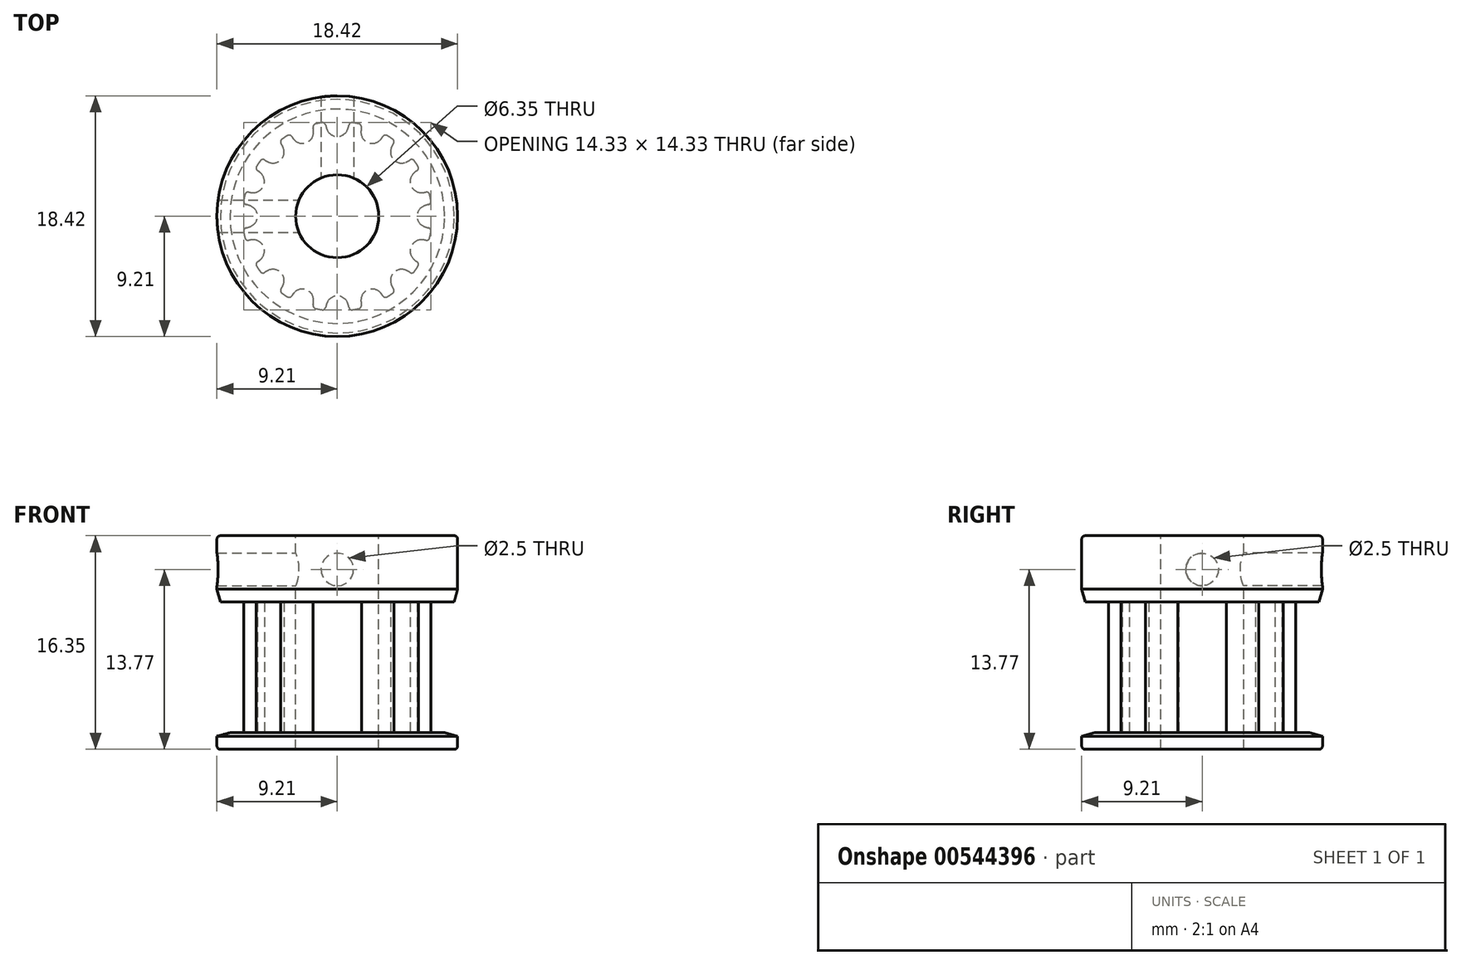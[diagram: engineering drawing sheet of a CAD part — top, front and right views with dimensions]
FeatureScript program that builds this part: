
annotation { "Feature Type Name" : "Feature", "Feature Type Description" : "" }
export const myFeature = defineFeature(function(context is Context, id is Id, definition is map)
    precondition{}
    {
        {
            assignVariable(context, id + "F0", {"name" : "teeth", "anyValue" : 16});
        }
        {
            assignVariable(context, id + "F1", {"name" : "width", "anyValue" : 10});
        }
        {
            var Q0;
            Q0=qCreatedBy(makeId("Top.planeOp"),FACE);
            var sketch = newSketch(context, id + "F2", { "sketchPlane" : qUnion([Q0])});
            skLineSegment(sketch, "E0", {"start": v(0, 0) * mm, "end": v(0, 6.1) * mm, "construction": true});
            skArc(sketch, "E1", {"start": v(1.86, 7.02) * mm, "mid": v(0, 7.26) * mm, "end": v(-1.86, 7.02) * mm, "construction": true});
            skArc(sketch, "E2", {"start": v(0, 6.1) * mm, "mid": v(0.46, 6.24) * mm, "end": v(0.77, 6.6) * mm});
            skLineSegment(sketch, "E3", {"start": v(0, 6.1) * mm, "end": v(0, 7.26) * mm, "construction": true});
            skLineSegment(sketch, "E4", {"start": v(0, 7.26) * mm, "end": v(0, 7.64) * mm, "construction": true});
            skArc(sketch, "E5", {"start": v(1.5, 7.5) * mm, "mid": v(0, 7.64) * mm, "end": v(-1.5, 7.5) * mm, "construction": true});
            skLineSegment(sketch, "E6", {"start": v(1.42, 7.12) * mm, "end": v(0, 0) * mm});
            skLineSegment(sketch, "E7", {"start": v(0, 0) * mm, "end": v(-1.42, 7.12) * mm});
            skArc(sketch, "E8", {"start": v(1.17, 7.16) * mm, "mid": v(0.99, 7.12) * mm, "end": v(0.89, 6.96) * mm});
            skArc(sketch, "E9", {"start": v(0.77, 6.6) * mm, "mid": v(0.84, 6.78) * mm, "end": v(0.89, 6.96) * mm});
            skArc(sketch, "E10.MirrorCS", {"start": v(0, 6.1) * mm, "mid": v(-0.46, 6.24) * mm, "end": v(-0.77, 6.6) * mm});
            skArc(sketch, "E11.MirrorCS", {"start": v(-0.77, 6.6) * mm, "mid": v(-0.84, 6.78) * mm, "end": v(-0.89, 6.96) * mm});
            skArc(sketch, "E12.MirrorCS", {"start": v(-1.17, 7.16) * mm, "mid": v(-0.99, 7.12) * mm, "end": v(-0.89, 6.96) * mm});
            skArc(sketch, "E13", {"start": v(0, 7.26) * mm, "mid": v(-0.3, 7.25) * mm, "end": v(-0.6, 7.23) * mm, "construction": true});
            skArc(sketch, "E14", {"start": v(1.65, 5.88) * mm, "mid": v(0, 6.1) * mm, "end": v(-1.65, 5.88) * mm, "construction": true});
            skArc(sketch, "E15", {"start": v(-1.17, 7.16) * mm, "mid": v(-1.3, 7.14) * mm, "end": v(-1.42, 7.12) * mm});
            skArc(sketch, "E16", {"start": v(1.17, 7.16) * mm, "mid": v(1.3, 7.14) * mm, "end": v(1.42, 7.12) * mm});
            skPoint(sketch, "E17", {"position": v(0, 6.1) * mm});
            skSolve(sketch);
        }
        {
            var Q0;
            Q0=makeQuery(id+"F2.imprint","IMPRINT",FACE,{"disambiguationData":[TD([[makeQuery(id+"F2.imprint","IMPRINT",EDGE,{"derivedFrom":sQuery(id+"F2.wireOp",EDGE,"E2")}),-1.0]])]});
            var Q1;
            {var subQ1=sQuery(id+"F2.wireOp",EDGE,"N9a9pOVT-NxnP-9PMo-Yz0L-ytRW1WlfzG62");Q1=makeQuery(id+"F2.imprint","IMPRINT",FACE,{"disambiguationData":[TD([[makeQuery(id+"F2.imprint","IMPRINT",EDGE,{"derivedFrom":subQ1}),-1.0]])]});}
            var Q2;
            {var subQ0=sQuery(id+"F2.wireOp",EDGE,"E6");Q2=makeQuery(id+"F2.imprint","IMPRINT",FACE,{"disambiguationData":[TD([[makeQuery(id+"F2.imprint","IMPRINT",EDGE,{"derivedFrom":subQ0}),-1.0]])]});}
            extrude(context, id + "F3", {"entities" : qUnion([Q0, Q1, Q2]), "depth" : (getVariable(context, 'width')) * mm, "offsetDistance" : 25 * mm, "symmetric" : true});
        }
        {
            var Q0;
            Q0=makeQuery(id+"F3.opExtrude","SWEPT_BODY",BODY,{"disambiguationData":[OSD([sQuery(id+"F2.wireOp",EDGE,"E1"),sQuery(id+"F2.wireOp",EDGE,"E2"),sQuery(id+"F2.wireOp",EDGE,"WtW3y5By-gfdo-wMA2-XeKf-OYMCoWhlFWBV"),sQuery(id+"F2.wireOp",EDGE,"E6"),sQuery(id+"F2.wireOp",EDGE,"E7"),sQuery(id+"F2.wireOp",EDGE,"N9a9pOVT-NxnP-9PMo-Yz0L-ytRW1WlfzG62"),sQuery(id+"F2.wireOp",EDGE,"E8"),sQuery(id+"F2.wireOp",EDGE,"E9"),sQuery(id+"F2.wireOp",EDGE,"E10.MirrorCS"),sQuery(id+"F2.wireOp",EDGE,"E11.MirrorCS"),sQuery(id+"F2.wireOp",EDGE,"E12.MirrorCS")])]});
            var Q1;
            Q1=makeQuery(id+"F3.opExtrude","SWEPT_EDGE",EDGE,{"disambiguationData":[OSD([sQuery(id+"F2.wireOp",EDGE,"E6"),sQuery(id+"F2.wireOp",EDGE,"E7")])]});
            circularPattern(context, id + "F4", {"operationType" : NewBodyOperationType.ADD, "entities" : qUnion([Q0]), "axis" : qUnion([Q1]), "angle" : 360 * degree, "instanceCount" : getVariable(context, 'teeth'), "equalSpace" : true});
        }
        {
            var Q0;
            {var subQ0=makeQuery(id+"F3.opExtrude","CAP_FACE",FACE,{"disambiguationData":[OSD([sQuery(id+"F2.wireOp",EDGE,"E2"),sQuery(id+"F2.wireOp",EDGE,"E6"),sQuery(id+"F2.wireOp",EDGE,"E7"),sQuery(id+"F2.wireOp",EDGE,"E8"),sQuery(id+"F2.wireOp",EDGE,"E9"),sQuery(id+"F2.wireOp",EDGE,"E10.MirrorCS"),sQuery(id+"F2.wireOp",EDGE,"E11.MirrorCS"),sQuery(id+"F2.wireOp",EDGE,"E12.MirrorCS"),sQuery(id+"F2.wireOp",EDGE,"E15"),sQuery(id+"F2.wireOp",EDGE,"E16")])],"isStart":true});Q0=makeQuery(id+"F4.boolean.opBoolean","MERGE",FACE,{"derivedFrom":[subQ0,makeQuery(id+"F4.opPattern","COPY",FACE,{"derivedFrom":subQ0,"instanceName":"1"}),makeQuery(id+"F4.opPattern","COPY",FACE,{"derivedFrom":subQ0,"instanceName":"2"}),makeQuery(id+"F4.opPattern","COPY",FACE,{"derivedFrom":subQ0,"instanceName":"3"}),makeQuery(id+"F4.opPattern","COPY",FACE,{"derivedFrom":subQ0,"instanceName":"4"}),makeQuery(id+"F4.opPattern","COPY",FACE,{"derivedFrom":subQ0,"instanceName":"5"}),makeQuery(id+"F4.opPattern","COPY",FACE,{"derivedFrom":subQ0,"instanceName":"6"}),makeQuery(id+"F4.opPattern","COPY",FACE,{"derivedFrom":subQ0,"instanceName":"7"}),makeQuery(id+"F4.opPattern","COPY",FACE,{"derivedFrom":subQ0,"instanceName":"8"}),makeQuery(id+"F4.opPattern","COPY",FACE,{"derivedFrom":subQ0,"instanceName":"9"}),makeQuery(id+"F4.opPattern","COPY",FACE,{"derivedFrom":subQ0,"instanceName":"10"}),makeQuery(id+"F4.opPattern","COPY",FACE,{"derivedFrom":subQ0,"instanceName":"11"}),makeQuery(id+"F4.opPattern","COPY",FACE,{"derivedFrom":subQ0,"instanceName":"12"}),makeQuery(id+"F4.opPattern","COPY",FACE,{"derivedFrom":subQ0,"instanceName":"13"}),makeQuery(id+"F4.opPattern","COPY",FACE,{"derivedFrom":subQ0,"instanceName":"14"}),makeQuery(id+"F4.opPattern","COPY",FACE,{"derivedFrom":subQ0,"instanceName":"15"}),makeQuery(id+"F4.opPattern","COPY",FACE,{"derivedFrom":subQ0,"instanceName":"16"}),makeQuery(id+"F4.opPattern","COPY",FACE,{"derivedFrom":subQ0,"instanceName":"17"}),makeQuery(id+"F4.opPattern","COPY",FACE,{"derivedFrom":subQ0,"instanceName":"18"}),makeQuery(id+"F4.opPattern","COPY",FACE,{"derivedFrom":subQ0,"instanceName":"19"}),makeQuery(id+"F4.opPattern","COPY",FACE,{"derivedFrom":subQ0,"instanceName":"20"}),makeQuery(id+"F4.opPattern","COPY",FACE,{"derivedFrom":subQ0,"instanceName":"21"}),makeQuery(id+"F4.opPattern","COPY",FACE,{"derivedFrom":subQ0,"instanceName":"22"}),makeQuery(id+"F4.opPattern","COPY",FACE,{"derivedFrom":subQ0,"instanceName":"23"}),makeQuery(id+"F4.opPattern","COPY",FACE,{"derivedFrom":subQ0,"instanceName":"24"}),makeQuery(id+"F4.opPattern","COPY",FACE,{"derivedFrom":subQ0,"instanceName":"25"}),makeQuery(id+"F4.opPattern","COPY",FACE,{"derivedFrom":subQ0,"instanceName":"26"}),makeQuery(id+"F4.opPattern","COPY",FACE,{"derivedFrom":subQ0,"instanceName":"27"}),makeQuery(id+"F4.opPattern","COPY",FACE,{"derivedFrom":subQ0,"instanceName":"28"}),makeQuery(id+"F4.opPattern","COPY",FACE,{"derivedFrom":subQ0,"instanceName":"29"}),makeQuery(id+"F4.opPattern","COPY",FACE,{"derivedFrom":subQ0,"instanceName":"30"}),makeQuery(id+"F4.opPattern","COPY",FACE,{"derivedFrom":subQ0,"instanceName":"31"}),makeQuery(id+"F4.opPattern","COPY",FACE,{"derivedFrom":subQ0,"instanceName":"32"}),makeQuery(id+"F4.opPattern","COPY",FACE,{"derivedFrom":subQ0,"instanceName":"33"}),makeQuery(id+"F4.opPattern","COPY",FACE,{"derivedFrom":subQ0,"instanceName":"34"}),makeQuery(id+"F4.opPattern","COPY",FACE,{"derivedFrom":subQ0,"instanceName":"35"}),makeQuery(id+"F4.opPattern","COPY",FACE,{"derivedFrom":subQ0,"instanceName":"36"}),makeQuery(id+"F4.opPattern","COPY",FACE,{"derivedFrom":subQ0,"instanceName":"37"}),makeQuery(id+"F4.opPattern","COPY",FACE,{"derivedFrom":subQ0,"instanceName":"38"}),makeQuery(id+"F4.opPattern","COPY",FACE,{"derivedFrom":subQ0,"instanceName":"39"})]});}
            var sketch = newSketch(context, id + "F5", { "sketchPlane" : qUnion([Q0])});
            skCircle(sketch, "E18", {"center": v(0, 0) * mm, "radius": 9.2 * mm});
            skSolve(sketch);
        }
        {
            var Q0;
            Q0=qSketchRegion(id+"F5",true);
            extrude(context, id + "F6", {"entities" : qUnion([Q0]), "operationType" : NewBodyOperationType.ADD, "depth" : 1.27 * mm, "offsetDistance" : 25 * mm});
        }
        {
            var Q0;
            {var subQ0=makeQuery(id+"F3.opExtrude","CAP_FACE",FACE,{"disambiguationData":[OSD([sQuery(id+"F2.wireOp",EDGE,"E2"),sQuery(id+"F2.wireOp",EDGE,"E6"),sQuery(id+"F2.wireOp",EDGE,"E7"),sQuery(id+"F2.wireOp",EDGE,"E8"),sQuery(id+"F2.wireOp",EDGE,"E9"),sQuery(id+"F2.wireOp",EDGE,"E10.MirrorCS"),sQuery(id+"F2.wireOp",EDGE,"E11.MirrorCS"),sQuery(id+"F2.wireOp",EDGE,"E12.MirrorCS"),sQuery(id+"F2.wireOp",EDGE,"E15"),sQuery(id+"F2.wireOp",EDGE,"E16")])],"isStart":false});Q0=makeQuery(id+"F4.boolean.opBoolean","MERGE",FACE,{"derivedFrom":[subQ0,makeQuery(id+"F4.opPattern","COPY",FACE,{"derivedFrom":subQ0,"instanceName":"1"}),makeQuery(id+"F4.opPattern","COPY",FACE,{"derivedFrom":subQ0,"instanceName":"2"}),makeQuery(id+"F4.opPattern","COPY",FACE,{"derivedFrom":subQ0,"instanceName":"3"}),makeQuery(id+"F4.opPattern","COPY",FACE,{"derivedFrom":subQ0,"instanceName":"4"}),makeQuery(id+"F4.opPattern","COPY",FACE,{"derivedFrom":subQ0,"instanceName":"5"}),makeQuery(id+"F4.opPattern","COPY",FACE,{"derivedFrom":subQ0,"instanceName":"6"}),makeQuery(id+"F4.opPattern","COPY",FACE,{"derivedFrom":subQ0,"instanceName":"7"}),makeQuery(id+"F4.opPattern","COPY",FACE,{"derivedFrom":subQ0,"instanceName":"8"}),makeQuery(id+"F4.opPattern","COPY",FACE,{"derivedFrom":subQ0,"instanceName":"9"}),makeQuery(id+"F4.opPattern","COPY",FACE,{"derivedFrom":subQ0,"instanceName":"10"}),makeQuery(id+"F4.opPattern","COPY",FACE,{"derivedFrom":subQ0,"instanceName":"11"}),makeQuery(id+"F4.opPattern","COPY",FACE,{"derivedFrom":subQ0,"instanceName":"12"}),makeQuery(id+"F4.opPattern","COPY",FACE,{"derivedFrom":subQ0,"instanceName":"13"}),makeQuery(id+"F4.opPattern","COPY",FACE,{"derivedFrom":subQ0,"instanceName":"14"}),makeQuery(id+"F4.opPattern","COPY",FACE,{"derivedFrom":subQ0,"instanceName":"15"}),makeQuery(id+"F4.opPattern","COPY",FACE,{"derivedFrom":subQ0,"instanceName":"16"}),makeQuery(id+"F4.opPattern","COPY",FACE,{"derivedFrom":subQ0,"instanceName":"17"}),makeQuery(id+"F4.opPattern","COPY",FACE,{"derivedFrom":subQ0,"instanceName":"18"}),makeQuery(id+"F4.opPattern","COPY",FACE,{"derivedFrom":subQ0,"instanceName":"19"}),makeQuery(id+"F4.opPattern","COPY",FACE,{"derivedFrom":subQ0,"instanceName":"20"}),makeQuery(id+"F4.opPattern","COPY",FACE,{"derivedFrom":subQ0,"instanceName":"21"}),makeQuery(id+"F4.opPattern","COPY",FACE,{"derivedFrom":subQ0,"instanceName":"22"}),makeQuery(id+"F4.opPattern","COPY",FACE,{"derivedFrom":subQ0,"instanceName":"23"}),makeQuery(id+"F4.opPattern","COPY",FACE,{"derivedFrom":subQ0,"instanceName":"24"}),makeQuery(id+"F4.opPattern","COPY",FACE,{"derivedFrom":subQ0,"instanceName":"25"}),makeQuery(id+"F4.opPattern","COPY",FACE,{"derivedFrom":subQ0,"instanceName":"26"}),makeQuery(id+"F4.opPattern","COPY",FACE,{"derivedFrom":subQ0,"instanceName":"27"}),makeQuery(id+"F4.opPattern","COPY",FACE,{"derivedFrom":subQ0,"instanceName":"28"}),makeQuery(id+"F4.opPattern","COPY",FACE,{"derivedFrom":subQ0,"instanceName":"29"}),makeQuery(id+"F4.opPattern","COPY",FACE,{"derivedFrom":subQ0,"instanceName":"30"}),makeQuery(id+"F4.opPattern","COPY",FACE,{"derivedFrom":subQ0,"instanceName":"31"}),makeQuery(id+"F4.opPattern","COPY",FACE,{"derivedFrom":subQ0,"instanceName":"32"}),makeQuery(id+"F4.opPattern","COPY",FACE,{"derivedFrom":subQ0,"instanceName":"33"}),makeQuery(id+"F4.opPattern","COPY",FACE,{"derivedFrom":subQ0,"instanceName":"34"}),makeQuery(id+"F4.opPattern","COPY",FACE,{"derivedFrom":subQ0,"instanceName":"35"}),makeQuery(id+"F4.opPattern","COPY",FACE,{"derivedFrom":subQ0,"instanceName":"36"}),makeQuery(id+"F4.opPattern","COPY",FACE,{"derivedFrom":subQ0,"instanceName":"37"}),makeQuery(id+"F4.opPattern","COPY",FACE,{"derivedFrom":subQ0,"instanceName":"38"}),makeQuery(id+"F4.opPattern","COPY",FACE,{"derivedFrom":subQ0,"instanceName":"39"})]});}
            var sketch = newSketch(context, id + "F7", { "sketchPlane" : qUnion([Q0])});
            skCircle(sketch, "E19", {"center": v(0, 0) * mm, "radius": 9.2 * mm});
            skSolve(sketch);
        }
        {
            var Q0;
            Q0=qSketchRegion(id+"F7",true);
            extrude(context, id + "F8", {"entities" : qUnion([Q0]), "operationType" : NewBodyOperationType.ADD, "depth" : 1.27 * mm, "offsetDistance" : 25 * mm});
        }
        {
            var Q0;
            Q0=makeQuery(id+"F8.opExtrude","CAP_FACE",FACE,{"disambiguationData":[OSD([sQuery(id+"F7.wireOp",EDGE,"E19")])],"isStart":false});
            var sketch = newSketch(context, id + "F9", { "sketchPlane" : qUnion([Q0])});
            skCircle(sketch, "E20", {"center": v(0, 0) * mm, "radius": 9.2 * mm});
            skSolve(sketch);
        }
        {
            var Q0;
            Q0=qSketchRegion(id+"F9",true);
            extrude(context, id + "F10", {"entities" : qUnion([Q0]), "operationType" : NewBodyOperationType.ADD, "depth" : 3.81 * mm, "offsetDistance" : 25 * mm});
        }
        {
            var Q0;
            Q0=makeQuery(id+"F10.opExtrude","CAP_FACE",FACE,{"disambiguationData":[OSD([sQuery(id+"F9.wireOp",EDGE,"E20")])],"isStart":false});
            var sketch = newSketch(context, id + "F11", { "sketchPlane" : qUnion([Q0])});
            skCircle(sketch, "E21", {"center": v(0, 0) * mm, "radius": 3.18 * mm});
            skSolve(sketch);
        }
        {
            var Q0;
            Q0=qSketchRegion(id+"F11",true);
            extrude(context, id + "F12", {"entities" : qUnion([Q0]), "operationType" : NewBodyOperationType.REMOVE, "endBound" : BoundingType.THROUGH_ALL, "oppositeDirection" : true, "depth" : 25 * mm, "offsetDistance" : 25 * mm});
        }
        {
            var Q0;
            Q0=qCreatedBy(makeId("Front.planeOp"),FACE);
            var sketch = newSketch(context, id + "F13", { "sketchPlane" : qUnion([Q0])});
            skCircle(sketch, "E22", {"center": v(0, 7.5) * mm, "radius": 1.25 * mm});
            skSolve(sketch);
        }
        {
            var Q0;
            Q0=qSketchRegion(id+"F13",true);
            extrude(context, id + "F14", {"entities" : qUnion([Q0]), "operationType" : NewBodyOperationType.REMOVE, "endBound" : BoundingType.THROUGH_ALL, "oppositeDirection" : true, "depth" : 25 * mm, "offsetDistance" : 25 * mm});
        }
        {
            var Q0;
            Q0=qCreatedBy(makeId("Right.planeOp"),FACE);
            var sketch = newSketch(context, id + "F15", { "sketchPlane" : qUnion([Q0])});
            skCircle(sketch, "E23", {"center": v(0, 7.5) * mm, "radius": 1.25 * mm});
            skSolve(sketch);
        }
        {
            var Q0;
            Q0=qSketchRegion(id+"F15",true);
            extrude(context, id + "F16", {"entities" : qUnion([Q0]), "operationType" : NewBodyOperationType.REMOVE, "endBound" : BoundingType.THROUGH_ALL, "oppositeDirection" : true, "depth" : 25 * mm, "offsetDistance" : 25 * mm});
        }
        {
            var Q0;
            Q0=makeQuery(id+"F6.opExtrude","CAP_EDGE",EDGE,{"disambiguationData":[OSD([sQuery(id+"F5.wireOp",EDGE,"E18")])],"isStart":true});
            var Q1;
            Q1=makeQuery(id+"F8.opExtrude","CAP_EDGE",EDGE,{"disambiguationData":[OSD([sQuery(id+"F7.wireOp",EDGE,"E19")])],"isStart":true});
            chamfer(context, id + "F17", {"entities" : qUnion([Q0, Q1]), "chamferType" : ChamferType.OFFSET_ANGLE, "width" : 1 * mm, "oppositeDirection" : true, "angle" : 15 * degree, "tangentPropagation" : true});
        }
        {
            var Q0;
            Q0=makeQuery(id+"F10.opExtrude","CAP_EDGE",EDGE,{"disambiguationData":[OSD([sQuery(id+"F9.wireOp",EDGE,"E20")])],"isStart":true});
            var Q1;
            Q1=makeQuery(id+"F10.opExtrude","CAP_EDGE",EDGE,{"disambiguationData":[OSD([sQuery(id+"F9.wireOp",EDGE,"E20")])],"isStart":false});
            var Q2;
            Q2=makeQuery(id+"F8.opExtrude","CAP_EDGE",EDGE,{"disambiguationData":[OSD([sQuery(id+"F7.wireOp",EDGE,"E19")])],"isStart":false});
            var Q3;
            Q3=makeQuery(id+"F6.opExtrude","CAP_EDGE",EDGE,{"disambiguationData":[OSD([sQuery(id+"F5.wireOp",EDGE,"E18")])],"isStart":false});
            fillet(context, id + "F18", {"entities" : qUnion([Q0, Q1, Q2, Q3]), "radius" : 0.25 * mm, "tangentPropagation" : true, "allowEdgeOverflow" : false});
        }
    });
